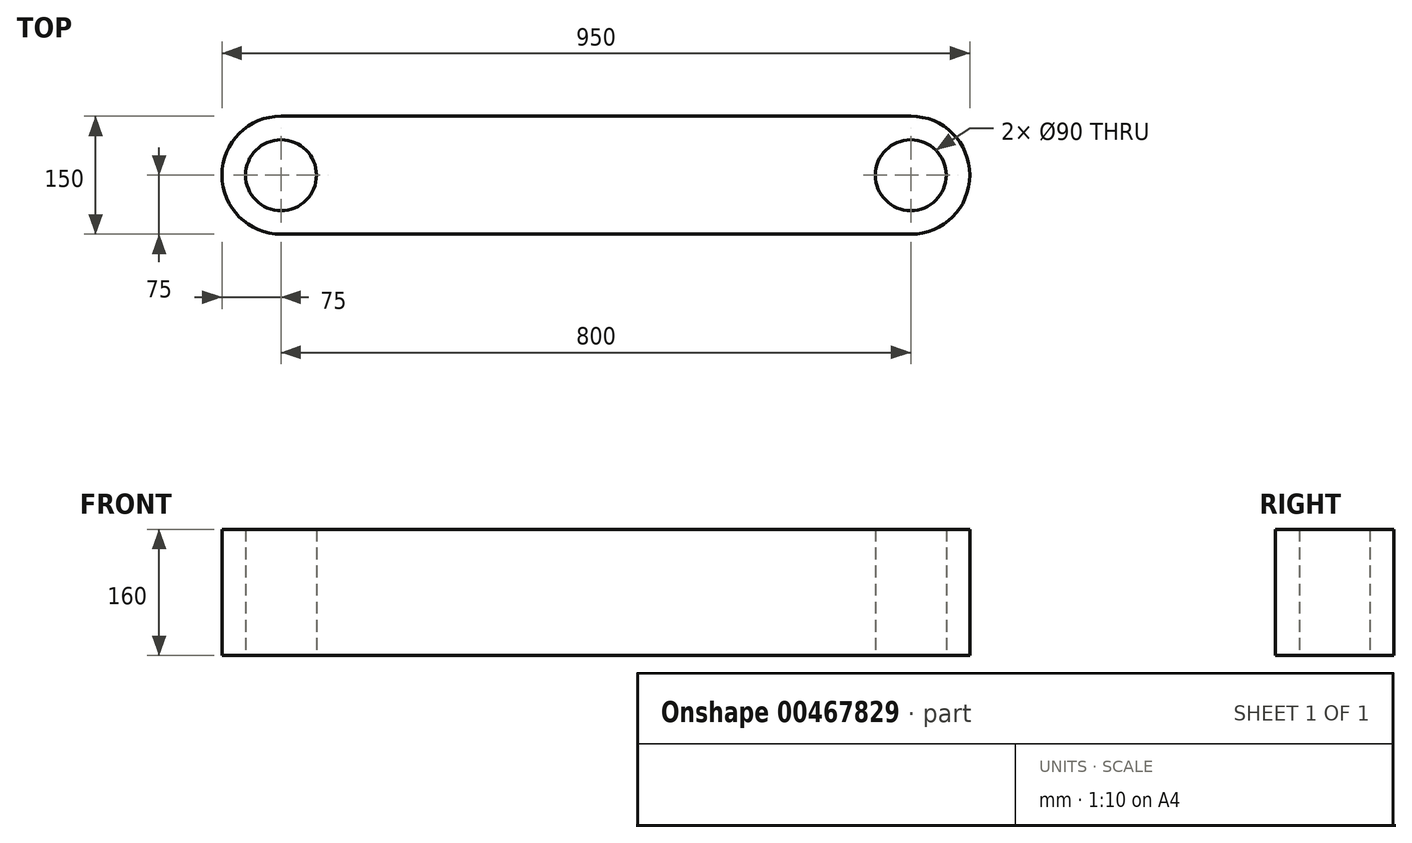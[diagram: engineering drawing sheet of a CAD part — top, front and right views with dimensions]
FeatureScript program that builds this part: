
annotation { "Feature Type Name" : "Feature", "Feature Type Description" : "" }
export const myFeature = defineFeature(function(context is Context, id is Id, definition is map)
    precondition{}
    {
        {
            var Q0;
            Q0=qCreatedBy(makeId("Top.planeOp"),FACE);
            var sketch = newSketch(context, id + "F0", { "sketchPlane" : qUnion([Q0])});
            skArc(sketch, "E0", {"start": v(0, 75) * mm, "mid": v(-75, 0) * mm, "end": v(0, -75) * mm});
            skLineSegment(sketch, "E1", {"start": v(0, 75) * mm, "end": v(800, 75) * mm});
            skLineSegment(sketch, "E2", {"start": v(800, 75) * mm, "end": v(800, -75) * mm});
            skLineSegment(sketch, "E3", {"start": v(800, -75) * mm, "end": v(0, -75) * mm});
            skArc(sketch, "E4", {"start": v(800, -75) * mm, "mid": v(875, 0) * mm, "end": v(800, 75) * mm});
            skSolve(sketch);
        }
        {
            var Q0;
            Q0 = qSketchRegion(id + "F0", true);
            extrude(context, id + "F1", {"entities" : qUnion([Q0]), "depth" : 160 * mm});
        }
        {
            var Q0;
            Q0=makeQuery(id+"F1.opExtrude","CAP_FACE",FACE,{"disambiguationData":[OSD([sQuery(id+"F0.wireOp",EDGE,"E0"),sQuery(id+"F0.wireOp",EDGE,"E1"),sQuery(id+"F0.wireOp",EDGE,"E3"),sQuery(id+"F0.wireOp",EDGE,"E4")])],"isStart":true});
            var sketch = newSketch(context, id + "F2", { "sketchPlane" : qUnion([Q0])});
            skCircle(sketch, "E5", {"center": v(0, 0) * mm, "radius": 45 * mm});
            skCircle(sketch, "E6", {"center": v(800, 0) * mm, "radius": 45 * mm});
            skSolve(sketch);
        }
        {
            var Q0;
            Q0 = qSketchRegion(id + "F2", true);
            extrude(context, id + "F3", {"entities" : qUnion([Q0]), "operationType" : NewBodyOperationType.REMOVE, "oppositeDirection" : true, "depth" : 291 * mm});
        }
    });
